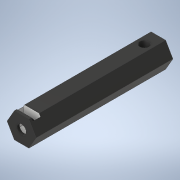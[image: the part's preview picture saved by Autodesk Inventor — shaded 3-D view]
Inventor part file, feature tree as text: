
AUTODESK INVENTOR PART (.ipt)
format: ipt  version: 2020 (Build 240168000, 168)  size: 226,304 bytes
history: native  units: mm
features: extrude x11, sketch x11, projected_geometry x6, plane x1, mirror x1
ambient origin geometry x8: Origin, YZ Plane, XZ Plane, XY Plane, X Axis, Y Axis, Z Axis, Center Point
bodies: Solid1 (feature_tree)
feature tree (30):
  extrude  "Extrusion1"  Depth=44.0mm TaperAngle=0.0deg
  extrude  "Extrusion2"  Depth=5.6mm
  extrude  "Extrusion3"  Depth=3.0mm
  plane  "Work Plane1"
  mirror  "Mirror1"
  extrude  "Extrusion4"  TaperAngle=0.0deg  [1 undecoded]
  extrude  "Extrusion5"  TaperAngle=120.0deg  [1 undecoded]
  extrude  "Extrusion6"  Depth=9.5mm TaperAngle=0.0deg
  extrude  "Extrusion8"  Depth=5.6mm
  extrude  "Extrusion9"  Depth=6.0mm TaperAngle=0.0deg
  extrude  "Extrusion10"  TaperAngle=120.0deg  [1 undecoded]
  extrude  "Extrusion11"  Depth=1.9345mm
  extrude  "Extrusion12"  Depth=2.5mm
  sketch  "Sketch1"  dims[d0=4.05mm d1=44.0mm d2=0.0mm]
  sketch  "Sketch2"  dims[d3=2.5mm d4=5.6mm]
  sketch  "Sketch3"  dims[d5=6.0mm d6=0.0mm d7=3.0mm]
  sketch  "Sketch4"  dims[d8=8.0mm d9=0.0mm d10=0.0mm]
  sketch  "Sketch5"  dims[d11=6.0mm d12=120.0deg]
  projected_geometry  "Projected Loop1"
  projected_geometry  "Projected Loop2"
  sketch  "Sketch6"  dims[d13=120.0deg d14=9.5mm d15=0.0mm]
  sketch  "Sketch8"  dims[d16=2.5mm d17=5.6mm]
  sketch  "Sketch9"  dims[d18=6.0mm d19=6.0mm d20=0.0mm]
  projected_geometry  "Projected Loop4"
  sketch  "Sketch10"  dims[d21=120.0deg d22=120.0deg]
  projected_geometry  "Projected Loop5"
  sketch  "Sketch11"  dims[d23=6.0mm d24=0.0mm d25=1.9345mm]
  projected_geometry  "Projected Loop6"
  sketch  "Sketch12"  dims[d32=5.6mm d33=2.5mm d34=6.5mm d35=0.0mm d36=90.0deg d37=3.0mm d38=0.0mm d39=4.5mm d40=8.0mm d41=0.0mm d42=30.0deg d43=150.0deg d44=2.5mm d45=0.0mm d46=5.6mm d47=2.5mm d48=2.05mm d50=5.85mm d51=0.0mm d52=150.0deg d53=30.0deg d54=5.75mm d55=0.0mm]
  projected_geometry  "Projected Loop7"
note: 3 required parameter values undecoded (feature->parameter linkage not recoverable at this tier; creation-order binding heuristic only, values carry confidence <= 0.55)
